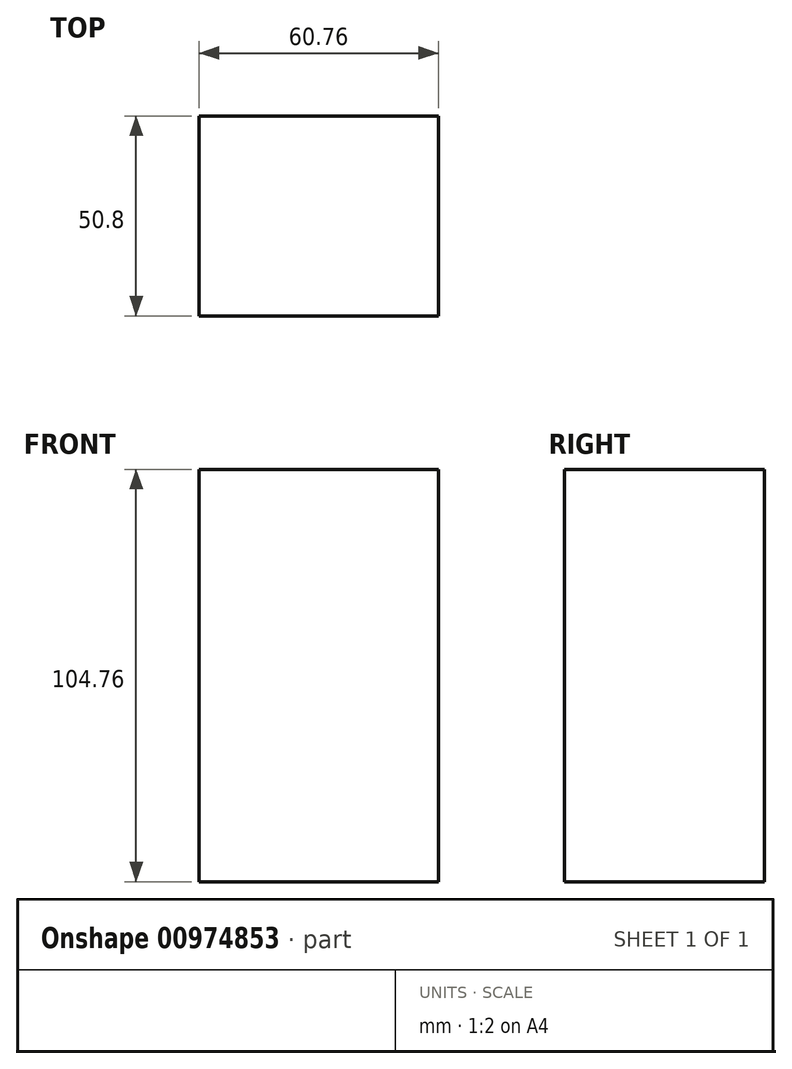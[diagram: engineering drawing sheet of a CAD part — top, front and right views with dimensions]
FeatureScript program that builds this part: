
annotation { "Feature Type Name" : "Feature", "Feature Type Description" : "" }
export const myFeature = defineFeature(function(context is Context, id is Id, definition is map)
    precondition{}
    {
        {
            var Q0;
            Q0=qCreatedBy(makeId("Front.planeOp"),FACE);
            var sketch = newSketch(context, id + "F0", { "sketchPlane" : qUnion([Q0])});
            skLineSegment(sketch, "E0.bottom", {"start": v(-46.49, 27.24) * mm, "end": v(14.27, 27.24) * mm});
            skLineSegment(sketch, "E0.top", {"start": v(-46.49, -77.52) * mm, "end": v(14.27, -77.52) * mm});
            skLineSegment(sketch, "E0.left", {"start": v(-46.49, 27.24) * mm, "end": v(-46.49, -77.52) * mm});
            skLineSegment(sketch, "E0.right", {"start": v(14.27, 27.24) * mm, "end": v(14.27, -77.52) * mm});
            skSolve(sketch);
        }
        {
            var Q0;
            Q0=makeQuery(id+"F0.imprint","IMPRINT",FACE,{"disambiguationData":[TD([[makeQuery(id+"F0.imprint","IMPRINT",EDGE,{"derivedFrom":sQuery(id+"F0.wireOp",EDGE,"E0.bottom")}),-1.0]])]});
            extrude(context, id + "F1", {"entities" : qUnion([Q0]), "depth" : 50.8 * mm, "offsetDistance" : 25.4 * mm});
        }
    });
